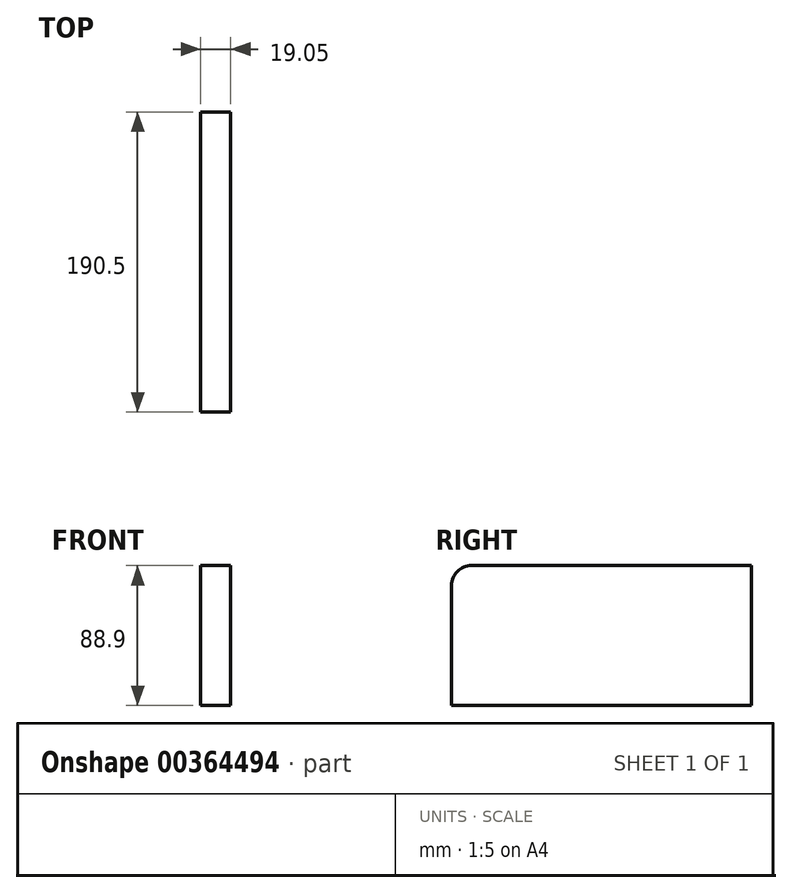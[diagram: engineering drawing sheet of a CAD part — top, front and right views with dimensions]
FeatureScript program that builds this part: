
annotation { "Feature Type Name" : "Feature", "Feature Type Description" : "" }
export const myFeature = defineFeature(function(context is Context, id is Id, definition is map)
    precondition{}
    {
        {
            var Q0;
            Q0=qCreatedBy(makeId("Right.planeOp"),FACE);
            var sketch = newSketch(context, id + "F0", { "sketchPlane" : qUnion([Q0])});
            skLineSegment(sketch, "E0.bottom", {"start": v(0, 0) * mm, "end": v(190.5, 0) * mm});
            skLineSegment(sketch, "E0.top", {"start": v(12.7, 88.9) * mm, "end": v(190.5, 88.9) * mm});
            skLineSegment(sketch, "E0.left", {"start": v(0, 0) * mm, "end": v(0, 76.2) * mm});
            skLineSegment(sketch, "E0.right", {"start": v(190.5, 0) * mm, "end": v(190.5, 88.9) * mm});
            skPoint(sketch, "E1.visualSharp", {"position": v(0, 88.9) * mm});
            skArc(sketch, "E1.filletArc", {"start": v(12.7, 88.9) * mm, "mid": v(3.72, 85.18) * mm, "end": v(0, 76.2) * mm});
            skSolve(sketch);
        }
        {
            var Q0;
            Q0=makeQuery(id+"F0.imprint","IMPRINT",FACE,{"disambiguationData":[TD([[makeQuery(id+"F0.imprint","IMPRINT",EDGE,{"derivedFrom":sQuery(id+"F0.wireOp",EDGE,"E0.bottom")}),1.0]])]});
            extrude(context, id + "F1", {"entities" : qUnion([Q0]), "depth" : 19.05 * mm});
        }
    });
